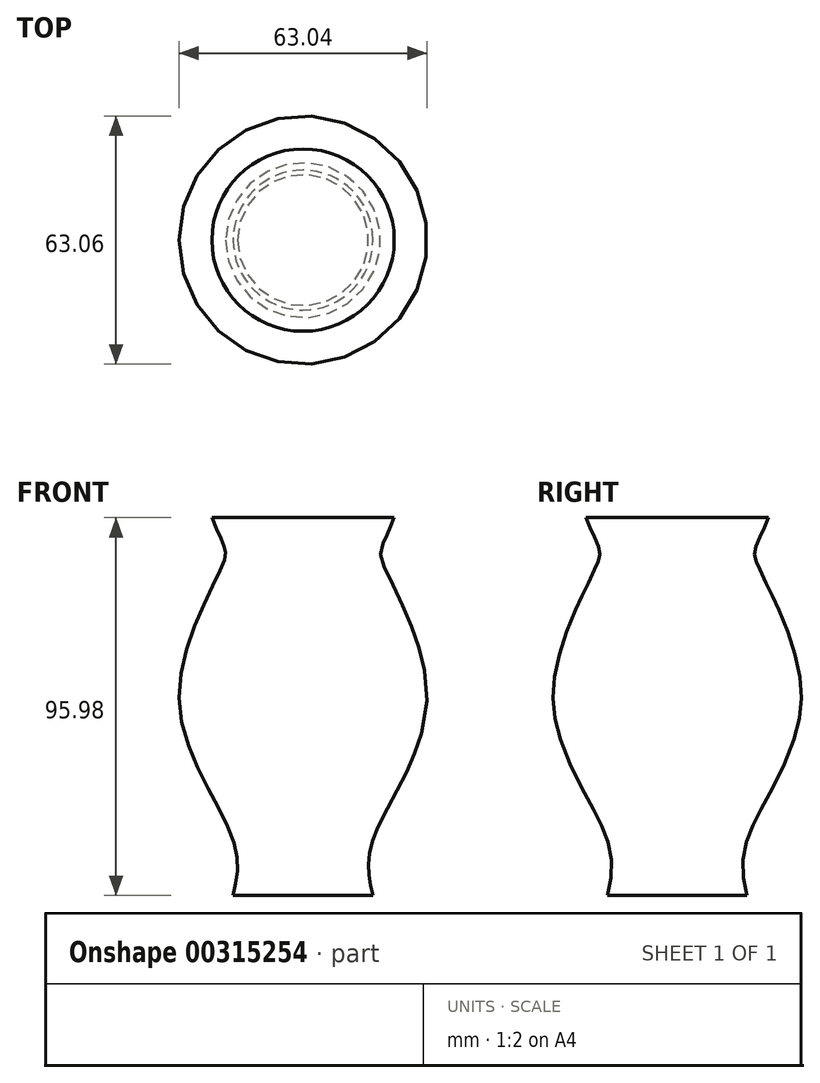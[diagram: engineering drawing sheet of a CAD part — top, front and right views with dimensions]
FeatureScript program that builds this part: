
annotation { "Feature Type Name" : "Feature", "Feature Type Description" : "" }
export const myFeature = defineFeature(function(context is Context, id is Id, definition is map)
    precondition{}
    {
        {
            var Q0;
            Q0=qCreatedBy(makeId("Front.planeOp"),FACE);
            var sketch = newSketch(context, id + "F0", { "sketchPlane" : qUnion([Q0])});
            skFitSpline(sketch, "E0", {"points": [v(17.77, 0) * mm, v(17.63, 13.83) * mm, v(31.53, 49.9) * mm, v(20.3, 84.3) * mm, v(19.96, 88.46) * mm, v(23.16, 95.98) * mm], "startDerivative": vector(-16.21, 71) * mm, "endDerivative": vector(26.75, 69.61) * mm});
            skLineSegment(sketch, "E1", {"start": v(17.77, 0) * mm, "end": v(0, 0) * mm});
            skLineSegment(sketch, "E2", {"start": v(0, 0) * mm, "end": v(0, 95.98) * mm});
            skLineSegment(sketch, "E3", {"start": v(0, 95.98) * mm, "end": v(23.16, 95.98) * mm});
            skSolve(sketch);
        }
        {
            var Q0;
            Q0=makeQuery(id+"F0.imprint","IMPRINT",FACE,{"disambiguationData":[TD([[makeQuery(id+"F0.imprint","IMPRINT",EDGE,{"derivedFrom":sQuery(id+"F0.wireOp",EDGE,"E0")}),1.0]])]});
            var Q1;
            Q1=sQuery(id+"F0.wireOp",EDGE,"E2");
            revolve(context, id + "F1", {"entities" : qUnion([Q0]), "axis" : qUnion([Q1]), "revolveType" : RevolveType.FULL});
        }
    });
